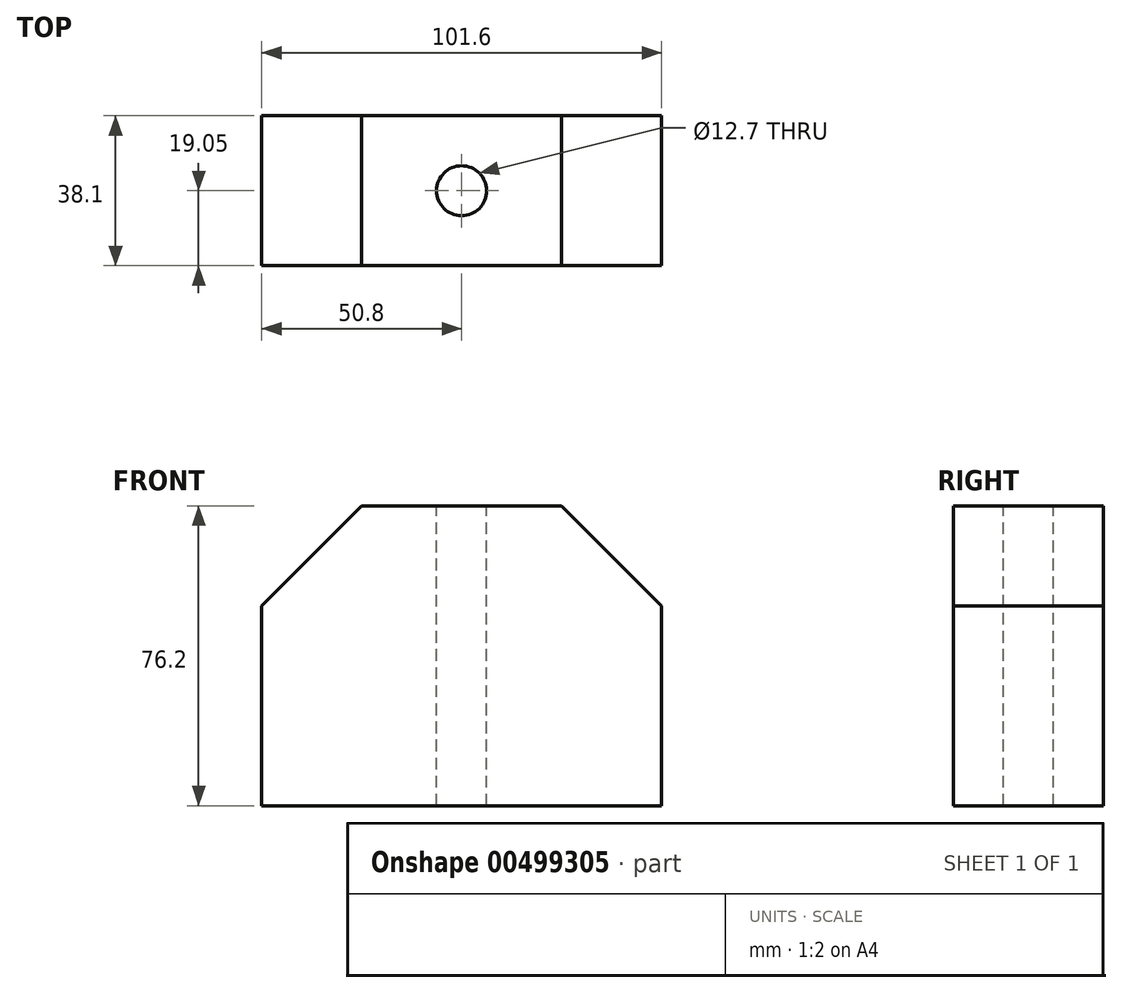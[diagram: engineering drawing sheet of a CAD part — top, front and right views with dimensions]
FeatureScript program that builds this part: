
annotation { "Feature Type Name" : "Feature", "Feature Type Description" : "" }
export const myFeature = defineFeature(function(context is Context, id is Id, definition is map)
    precondition{}
    {
        {
            var Q0;
            Q0=qCreatedBy(makeId("Front.planeOp"),FACE);
            var sketch = newSketch(context, id + "F0", { "sketchPlane" : qUnion([Q0])});
            skLineSegment(sketch, "E0", {"start": v(0, 0) * mm, "end": v(101.6, 0) * mm});
            skLineSegment(sketch, "E1", {"start": v(101.6, 0) * mm, "end": v(101.6, 50.8) * mm});
            skLineSegment(sketch, "E2", {"start": v(101.6, 50.8) * mm, "end": v(76.2, 76.2) * mm});
            skLineSegment(sketch, "E3", {"start": v(76.2, 76.2) * mm, "end": v(25.4, 76.2) * mm});
            skLineSegment(sketch, "E4", {"start": v(25.4, 76.2) * mm, "end": v(0, 50.8) * mm});
            skLineSegment(sketch, "E5", {"start": v(0, 50.8) * mm, "end": v(0, 0) * mm});
            skSolve(sketch);
        }
        {
            var Q0;
            Q0=makeQuery(id+"F0.imprint","IMPRINT",FACE,{"disambiguationData":[TD([[makeQuery(id+"F0.imprint","IMPRINT",EDGE,{"derivedFrom":sQuery(id+"F0.wireOp",EDGE,"E0")}),1.0]])]});
            extrude(context, id + "F1", {"entities" : qUnion([Q0]), "depth" : 38.1 * mm});
        }
        {
            var Q0;
            Q0=makeQuery(id+"F1.opExtrude","SWEPT_FACE",FACE,{"disambiguationData":[OSD([sQuery(id+"F0.wireOp",EDGE,"E3")])]});
            var sketch = newSketch(context, id + "F2", { "sketchPlane" : qUnion([Q0])});
            skLineSegment(sketch, "E6", {"start": v(50.8, -38.1) * mm, "end": v(50.8, -19.05) * mm});
            skPoint(sketch, "E6.endSnap0", {"position": v(76.2, -19.05) * mm});
            skCircle(sketch, "E7", {"center": v(50.8, -19.05) * mm, "radius": 6.35 * mm});
            skSolve(sketch);
        }
        {
            var Q0;
            Q0=makeQuery(id+"F2.imprint","IMPRINT",FACE,{"disambiguationData":[TD([[makeQuery(id+"F2.imprint","IMPRINT",EDGE,{"derivedFrom":sQuery(id+"F2.wireOp",EDGE,"E7")}),1.0]])]});
            extrude(context, id + "F3", {"entities" : qUnion([Q0]), "operationType" : NewBodyOperationType.REMOVE, "endBound" : BoundingType.THROUGH_ALL, "oppositeDirection" : true, "depth" : 25.4 * mm});
        }
    });
